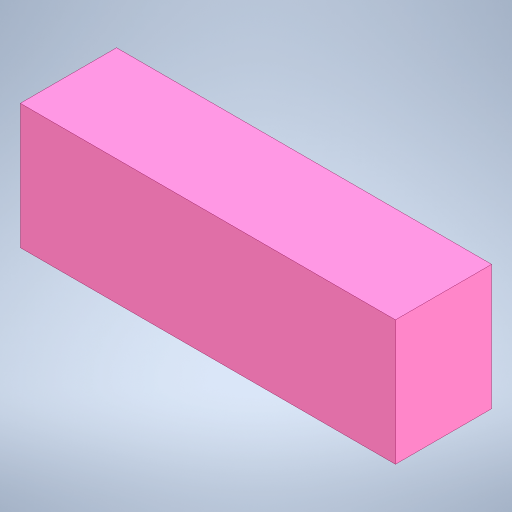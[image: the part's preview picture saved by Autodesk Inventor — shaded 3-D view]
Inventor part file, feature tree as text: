
AUTODESK INVENTOR PART (.ipt)
format: ipt  version: 2023 (Build 270158000, 158)  size: 180,224 bytes
history: native  units: mm
features: other x1, extrude x1, sketch x1
ambient origin geometry x8: Origin, YZ Plane, XZ Plane, XY Plane, X Axis, Y Axis, Z Axis, Center Point
bodies: Body1 (feature_tree)
feature tree (3):
  other  "Těleso1"
  extrude  "Vysunutí1"  Depth=19.5mm
  sketch  "Náčrt1"
